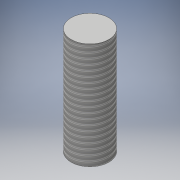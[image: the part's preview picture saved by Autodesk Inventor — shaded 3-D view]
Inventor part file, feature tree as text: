
AUTODESK INVENTOR PART (.ipt)
format: ipt  version: 2017.3 (Build 213256000, 256)  size: 102,400 bytes
history: native  units: in
note: dims shown in document units (in); Inventor stores cm internally (conversion verified against a paired STEP export)
features: extrude x1, thread x1, sketch x1
ambient origin geometry x8: Origin, YZ Plane, XZ Plane, XY Plane, X Axis, Y Axis, Z Axis, Center Point
bodies: Solid1 (feature_tree)
feature tree (3):
  extrude  "Extrusion1"  Depth=1.0in
  thread  "Thread2"  [1 undecoded]
  sketch  "Sketch1"  dims[d0=1.0in d1=0.0in d4=0.3543in d5=1.0in d6=0.0in]
note: 1 required parameter value undecoded (feature->parameter linkage not recoverable at this tier; creation-order binding heuristic only, values carry confidence <= 0.55)
